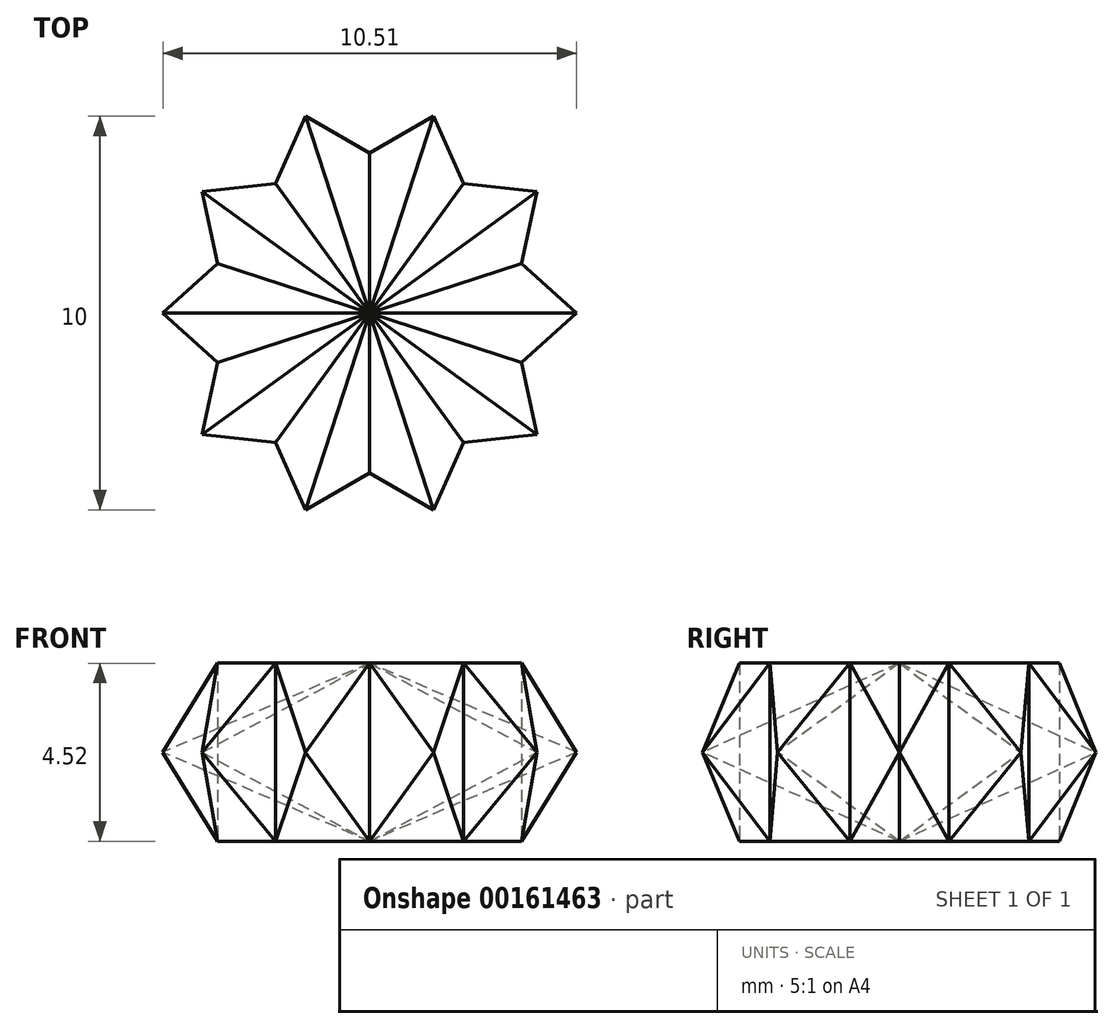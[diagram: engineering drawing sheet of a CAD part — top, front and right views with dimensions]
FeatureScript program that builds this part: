
annotation { "Feature Type Name" : "Feature", "Feature Type Description" : "" }
export const myFeature = defineFeature(function(context is Context, id is Id, definition is map)
    precondition{}
    {
        {
            var Q0;
            Q0=qCreatedBy(makeId("Top.planeOp"),FACE);
            var sketch = newSketch(context, id + "F0", { "sketchPlane" : qUnion([Q0])});
            skLineSegment(sketch, "E0", {"start": v(0, 0) * mm, "end": v(1.62, 5) * mm});
            skLineSegment(sketch, "E1", {"start": v(1.62, 5) * mm, "end": v(3.25, 0) * mm});
            skLineSegment(sketch, "E2", {"start": v(3.25, 0) * mm, "end": v(1.62, 0.94) * mm});
            skLineSegment(sketch, "E3", {"start": v(1.62, 0.94) * mm, "end": v(0, 0) * mm});
            skLineSegment(sketch, "E4", {"start": v(1.62, 5) * mm, "end": v(1.62, 0.94) * mm, "construction": true});
            skLineSegment(sketch, "E5", {"start": v(0, 0) * mm, "end": v(3.25, 0) * mm, "construction": true});
            skLineSegment(sketch, "E6", {"start": v(1.62, 0) * mm, "end": v(1.62, 5) * mm, "construction": true});
            skSolve(sketch);
        }
        {
            var Q0;
            Q0=qCreatedBy(makeId("Right.planeOp"),FACE);
            var sketch = newSketch(context, id + "F1", { "sketchPlane" : qUnion([Q0])});
            skPoint(sketch, "E7.0", {"position": v(0.94, 0) * mm});
            skPoint(sketch, "E8.0", {"position": v(5, 0) * mm});
            skLineSegment(sketch, "E9", {"start": v(0, 0) * mm, "end": v(5, 0) * mm});
            skLineSegment(sketch, "E10", {"start": v(0, 0) * mm, "end": v(0.94, 2.26) * mm});
            skLineSegment(sketch, "E11", {"start": v(0.94, 2.26) * mm, "end": v(5, 2.26) * mm});
            skLineSegment(sketch, "E12", {"start": v(5, 2.26) * mm, "end": v(5, 0) * mm});
            skSolve(sketch);
        }
        {
            var Q0;
            Q0=qCreatedBy(makeId("Front.planeOp"),FACE);
            var sketch = newSketch(context, id + "F2", { "sketchPlane" : qUnion([Q0])});
            skPoint(sketch, "E13.0", {"position": v(0, 2.26) * mm});
            skPoint(sketch, "E13.1", {"position": v(1.62, 0) * mm});
            skPoint(sketch, "E13.2", {"position": v(3.25, 0) * mm});
            skLineSegment(sketch, "E14", {"start": v(0, 0) * mm, "end": v(1.62, 2.26) * mm});
            skLineSegment(sketch, "E15", {"start": v(1.62, 2.26) * mm, "end": v(3.25, 0) * mm});
            skLineSegment(sketch, "E16", {"start": v(0, 0) * mm, "end": v(3.25, 0) * mm});
            skSolve(sketch);
        }
        {
            var Q0;
            Q0 = qSketchRegion(id + "F0", true);
            extrude(context, id + "F3", {"entities" : qUnion([Q0]), "depth" : 3 * mm});
        }
        {
            var Q0;
            Q0=makeQuery(id+"F1.imprint","IMPRINT",FACE,{"disambiguationData":[TD([[makeQuery(id+"F1.imprint","IMPRINT",EDGE,{"derivedFrom":sQuery(id+"F1.wireOp",EDGE,"E9")}),1.0]])]});
            extrude(context, id + "F4", {"entities" : qUnion([Q0]), "depth" : 4 * mm});
        }
        {
            var Q0;
            Q0 = qSketchRegion(id + "F2", true);
            extrude(context, id + "F5", {"entities" : qUnion([Q0]), "oppositeDirection" : true, "depth" : 5 * mm});
        }
        {
            var Q0;
            Q0=makeQuery(id+"F3.opExtrude","SWEPT_BODY",BODY,{"disambiguationData":[OSD([sQuery(id+"F0.wireOp",EDGE,"E0"),sQuery(id+"F0.wireOp",EDGE,"E1"),sQuery(id+"F0.wireOp",EDGE,"E2"),sQuery(id+"F0.wireOp",EDGE,"E3")])]});
            var Q1;
            Q1=makeQuery(id+"F5.opExtrude","SWEPT_BODY",BODY,{"disambiguationData":[OSD([sQuery(id+"F2.wireOp",EDGE,"E14"),sQuery(id+"F2.wireOp",EDGE,"E15"),sQuery(id+"F2.wireOp",EDGE,"E16")])]});
            booleanBodies(context, id + "F6", {"operationType" : BooleanOperationType.INTERSECTION, "tools" : qUnion([Q0, Q1])});
        }
        {
            var Q0;
            Q0=makeQuery(id+"F4.opExtrude","SWEPT_BODY",BODY,{"disambiguationData":[OSD([sQuery(id+"F1.wireOp",EDGE,"E9"),sQuery(id+"F1.wireOp",EDGE,"E10"),sQuery(id+"F1.wireOp",EDGE,"E11"),sQuery(id+"F1.wireOp",EDGE,"E12")])]});
            var Q1;
            Q1=makeQuery(id+"F6.opBoolean","INTERSECT",BODY,{"derivedFrom":[makeQuery(id+"F3.opExtrude","SWEPT_BODY",BODY,{"disambiguationData":[OSD([sQuery(id+"F0.wireOp",EDGE,"E0"),sQuery(id+"F0.wireOp",EDGE,"E1"),sQuery(id+"F0.wireOp",EDGE,"E2"),sQuery(id+"F0.wireOp",EDGE,"E3")])]}),makeQuery(id+"F5.opExtrude","SWEPT_BODY",BODY,{"disambiguationData":[OSD([sQuery(id+"F2.wireOp",EDGE,"E14"),sQuery(id+"F2.wireOp",EDGE,"E15"),sQuery(id+"F2.wireOp",EDGE,"E16")])]})]});
            booleanBodies(context, id + "F7", {"operationType" : BooleanOperationType.INTERSECTION, "tools" : qUnion([Q0, Q1])});
        }
        {
            var Q0;
            Q0=makeQuery(id+"F7.opBoolean","INTERSECT",BODY,{"derivedFrom":[makeQuery(id+"F4.opExtrude","SWEPT_BODY",BODY,{"disambiguationData":[OSD([sQuery(id+"F1.wireOp",EDGE,"E9"),sQuery(id+"F1.wireOp",EDGE,"E10"),sQuery(id+"F1.wireOp",EDGE,"E11"),sQuery(id+"F1.wireOp",EDGE,"E12")])]}),makeQuery(id+"F6.opBoolean","INTERSECT",BODY,{"derivedFrom":[makeQuery(id+"F3.opExtrude","SWEPT_BODY",BODY,{"disambiguationData":[OSD([sQuery(id+"F0.wireOp",EDGE,"E0"),sQuery(id+"F0.wireOp",EDGE,"E1"),sQuery(id+"F0.wireOp",EDGE,"E2"),sQuery(id+"F0.wireOp",EDGE,"E3")])]}),makeQuery(id+"F5.opExtrude","SWEPT_BODY",BODY,{"disambiguationData":[OSD([sQuery(id+"F2.wireOp",EDGE,"E14"),sQuery(id+"F2.wireOp",EDGE,"E15"),sQuery(id+"F2.wireOp",EDGE,"E16")])]})]})]});
            var Q1;
            Q1=makeQuery(id+"F4.opExtrude","SWEPT_FACE",FACE,{"disambiguationData":[OSD([sQuery(id+"F1.wireOp",EDGE,"E9")])]});
            mirror(context, id + "F8", {"operationType" : NewBodyOperationType.ADD, "entities" : qUnion([Q0]), "mirrorPlane" : qUnion([Q1])});
        }
        {
            var Q0;
            Q0=makeQuery(id+"F7.opBoolean","INTERSECT",BODY,{"derivedFrom":[makeQuery(id+"F4.opExtrude","SWEPT_BODY",BODY,{"disambiguationData":[OSD([sQuery(id+"F1.wireOp",EDGE,"E9"),sQuery(id+"F1.wireOp",EDGE,"E10"),sQuery(id+"F1.wireOp",EDGE,"E11"),sQuery(id+"F1.wireOp",EDGE,"E12")])]}),makeQuery(id+"F6.opBoolean","INTERSECT",BODY,{"derivedFrom":[makeQuery(id+"F3.opExtrude","SWEPT_BODY",BODY,{"disambiguationData":[OSD([sQuery(id+"F0.wireOp",EDGE,"E0"),sQuery(id+"F0.wireOp",EDGE,"E1"),sQuery(id+"F0.wireOp",EDGE,"E2"),sQuery(id+"F0.wireOp",EDGE,"E3")])]}),makeQuery(id+"F5.opExtrude","SWEPT_BODY",BODY,{"disambiguationData":[OSD([sQuery(id+"F2.wireOp",EDGE,"E14"),sQuery(id+"F2.wireOp",EDGE,"E15"),sQuery(id+"F2.wireOp",EDGE,"E16")])]})]})]});
            var Q1;
            {var subQ0=makeQuery(id+"F3.opExtrude","SWEPT_FACE",FACE,{"disambiguationData":[OSD([sQuery(id+"F0.wireOp",EDGE,"E1")])]});Q1=makeQuery(id+"F8.boolean.opBoolean","MERGE",FACE,{"derivedFrom":[subQ0,makeQuery(id+"F8.opPattern","COPY",FACE,{"derivedFrom":subQ0,"instanceName":"1"})]});}
            mirror(context, id + "F9", {"operationType" : NewBodyOperationType.ADD, "entities" : qUnion([Q0]), "mirrorPlane" : qUnion([Q1])});
        }
        {
            var Q0;
            Q0=makeQuery(id+"F7.opBoolean","INTERSECT",BODY,{"derivedFrom":[makeQuery(id+"F4.opExtrude","SWEPT_BODY",BODY,{"disambiguationData":[OSD([sQuery(id+"F1.wireOp",EDGE,"E9"),sQuery(id+"F1.wireOp",EDGE,"E10"),sQuery(id+"F1.wireOp",EDGE,"E11"),sQuery(id+"F1.wireOp",EDGE,"E12")])]}),makeQuery(id+"F6.opBoolean","INTERSECT",BODY,{"derivedFrom":[makeQuery(id+"F3.opExtrude","SWEPT_BODY",BODY,{"disambiguationData":[OSD([sQuery(id+"F0.wireOp",EDGE,"E0"),sQuery(id+"F0.wireOp",EDGE,"E1"),sQuery(id+"F0.wireOp",EDGE,"E2"),sQuery(id+"F0.wireOp",EDGE,"E3")])]}),makeQuery(id+"F5.opExtrude","SWEPT_BODY",BODY,{"disambiguationData":[OSD([sQuery(id+"F2.wireOp",EDGE,"E14"),sQuery(id+"F2.wireOp",EDGE,"E15"),sQuery(id+"F2.wireOp",EDGE,"E16")])]})]})]});
            var Q1;
            {var subQ0=makeQuery(id+"F3.opExtrude","SWEPT_FACE",FACE,{"disambiguationData":[OSD([sQuery(id+"F0.wireOp",EDGE,"E0")])]});Q1=makeQuery(id+"F9.opPattern","COPY",FACE,{"derivedFrom":makeQuery(id+"F8.boolean.opBoolean","MERGE",FACE,{"derivedFrom":[subQ0,makeQuery(id+"F8.opPattern","COPY",FACE,{"derivedFrom":subQ0,"instanceName":"1"})]}),"instanceName":"1"});}
            mirror(context, id + "F10", {"operationType" : NewBodyOperationType.ADD, "entities" : qUnion([Q0]), "mirrorPlane" : qUnion([Q1])});
        }
        {
            var Q0;
            Q0=makeQuery(id+"F7.opBoolean","INTERSECT",BODY,{"derivedFrom":[makeQuery(id+"F4.opExtrude","SWEPT_BODY",BODY,{"disambiguationData":[OSD([sQuery(id+"F1.wireOp",EDGE,"E9"),sQuery(id+"F1.wireOp",EDGE,"E10"),sQuery(id+"F1.wireOp",EDGE,"E11"),sQuery(id+"F1.wireOp",EDGE,"E12")])]}),makeQuery(id+"F6.opBoolean","INTERSECT",BODY,{"derivedFrom":[makeQuery(id+"F3.opExtrude","SWEPT_BODY",BODY,{"disambiguationData":[OSD([sQuery(id+"F0.wireOp",EDGE,"E0"),sQuery(id+"F0.wireOp",EDGE,"E1"),sQuery(id+"F0.wireOp",EDGE,"E2"),sQuery(id+"F0.wireOp",EDGE,"E3")])]}),makeQuery(id+"F5.opExtrude","SWEPT_BODY",BODY,{"disambiguationData":[OSD([sQuery(id+"F2.wireOp",EDGE,"E14"),sQuery(id+"F2.wireOp",EDGE,"E15"),sQuery(id+"F2.wireOp",EDGE,"E16")])]})]})]});
            var Q1;
            {var subQ0=makeQuery(id+"F3.opExtrude","SWEPT_FACE",FACE,{"disambiguationData":[OSD([sQuery(id+"F0.wireOp",EDGE,"E0")])]});Q1=makeQuery(id+"F10.opPattern","COPY",FACE,{"derivedFrom":makeQuery(id+"F8.boolean.opBoolean","MERGE",FACE,{"derivedFrom":[subQ0,makeQuery(id+"F8.opPattern","COPY",FACE,{"derivedFrom":subQ0,"instanceName":"1"})]}),"instanceName":"1"});}
            mirror(context, id + "F11", {"operationType" : NewBodyOperationType.ADD, "entities" : qUnion([Q0]), "mirrorPlane" : qUnion([Q1])});
        }
        {
            var Q0;
            Q0=makeQuery(id+"F7.opBoolean","INTERSECT",BODY,{"derivedFrom":[makeQuery(id+"F4.opExtrude","SWEPT_BODY",BODY,{"disambiguationData":[OSD([sQuery(id+"F1.wireOp",EDGE,"E9"),sQuery(id+"F1.wireOp",EDGE,"E10"),sQuery(id+"F1.wireOp",EDGE,"E11"),sQuery(id+"F1.wireOp",EDGE,"E12")])]}),makeQuery(id+"F6.opBoolean","INTERSECT",BODY,{"derivedFrom":[makeQuery(id+"F3.opExtrude","SWEPT_BODY",BODY,{"disambiguationData":[OSD([sQuery(id+"F0.wireOp",EDGE,"E0"),sQuery(id+"F0.wireOp",EDGE,"E1"),sQuery(id+"F0.wireOp",EDGE,"E2"),sQuery(id+"F0.wireOp",EDGE,"E3")])]}),makeQuery(id+"F5.opExtrude","SWEPT_BODY",BODY,{"disambiguationData":[OSD([sQuery(id+"F2.wireOp",EDGE,"E14"),sQuery(id+"F2.wireOp",EDGE,"E15"),sQuery(id+"F2.wireOp",EDGE,"E16")])]})]})]});
            var Q1;
            {var subQ0=makeQuery(id+"F3.opExtrude","SWEPT_FACE",FACE,{"disambiguationData":[OSD([sQuery(id+"F0.wireOp",EDGE,"E0")])]});Q1=makeQuery(id+"F8.boolean.opBoolean","MERGE",FACE,{"derivedFrom":[subQ0,makeQuery(id+"F8.opPattern","COPY",FACE,{"derivedFrom":subQ0,"instanceName":"1"})]});}
            mirror(context, id + "F12", {"operationType" : NewBodyOperationType.ADD, "entities" : qUnion([Q0]), "mirrorPlane" : qUnion([Q1])});
        }
    });
